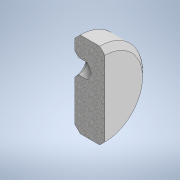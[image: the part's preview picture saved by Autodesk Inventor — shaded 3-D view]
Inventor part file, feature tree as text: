
AUTODESK INVENTOR PART (.ipt)
format: ipt  version: 2022 (Build 260153000, 153)  size: 125,952 bytes
history: native  units: mm
features: sketch x2, other x1, revolve x1, hole x1
ambient origin geometry x8: Origin, YZ Plane, XZ Plane, XY Plane, X Axis, Y Axis, Z Axis, Center Point
bodies: Body1 (feature_tree)
feature tree (5):
  other  "Твердое тело1"
  revolve  "Вращение1"
  hole  "Отверстие1"  [1 undecoded]
  sketch  "Эскиз1"
  sketch  "Эскиз2"
note: 1 required parameter value undecoded (feature->parameter linkage not recoverable at this tier; creation-order binding heuristic only, values carry confidence <= 0.55)
